# Revit family: Crealco Resistance Side Hung C
name_source: partatom
category: Windows
revit_build: Autodesk Revit 2016 (Build: 20150714_1515(x64)
units: mm (PartAtom-declared; Revit-internal decimal feet)

## family parameters
Always vertical = Yes
Cut with Voids When Loaded = No
Host = Wall
OmniClass Number = 23.30.20.00
OmniClass Title = Windows
Room Calculation Point = No
Shared = No

## types (5) — shared parameters
34mm Mullion Inertia = 3.901
50mm Mullion Inertia = 7.412
60mm Mullion Inertia = 10.935
70mm Mullion Inertia = 16.45
80mm Mullion Inertia = 23.166
90mm Mullion Inertia = 32.891
Default Sill Height = 800 mm
Description = Open Out Secure Window
Fixed Panel Mullion Gap = 15 mm  [stored 0.0492126 ft]
Fixed Panel Side Gap = 29 mm
Fixed Panel Transom Gap = 15 mm  [stored 0.0492126 ft]
Limit Fixed Panel Height Max = 6000 mm  [stored 19.685 ft]
Limit Fixed Panel Height Min = 100 mm  [stored 0.328084 ft]
Limit Fixed Panel Width Max = 6000 mm  [stored 19.685 ft]
Limit Fixed Panel Width Min = 100 mm  [stored 0.328084 ft]
Limit Glazing Thickness Max = 20 mm  [stored 0.0656168 ft]
Limit Glazing Thickness Min = 4 mm  [stored 0.0131234 ft]
Limit Mullion 1 Spacing Min = 230 mm  [stored 0.754593 ft]
Limit Sash Height Min = 200 mm  [stored 0.656168 ft]
Limit Sash Width Min = 200 mm  [stored 0.656168 ft]
Limit Window Height Min = 243 mm
Limit Window Width Min = 589 mm
Manufacturer = Crealco
Max Wind Load = 10000
Model = Resistance
Mullion Width = 20 mm  [stored 0.0656168 ft]
Sash Mullion Gap = 8 mm  [stored 0.0262467 ft]
Sash Offset = 4 mm  [stored 0.0131234 ft]
Sash Side Gap = 22 mm
Sash Transom Gap = 8 mm  [stored 0.0262467 ft]
Standard Mullion Side Gap = 595 mm  [stored 1.9521 ft]
Standard Transom 1 Top Gap = 595 mm  [stored 1.9521 ft]
Standard Transom 2 Top Gap = 582 mm  [stored 1.90945 ft]
Transom Mullion Side Gap = 15 mm  [stored 0.0492126 ft]
Transom Side Gap = 29 mm
URL = https://www.crealco.co.za
Wall Closure = By host
zero-valued in all types: Min Wind Load

## per-type parameters (varying)
| type | Standard Height | Standard Size | Standard Width | Type Comments |
| 1790 x 0890mm (RES-1809SS) | 890 mm  [stored 2.91995 ft] | Yes | 1790 mm  [stored 5.8727 ft] | RES-1809SS |
| User Defined | 890 mm  [stored 2.91995 ft] | No | 1790 mm  [stored 5.8727 ft] | Custom |
| 2390 x 0890mm (RES-2409SS) | 890 mm  [stored 2.91995 ft] | Yes | 2390 mm  [stored 7.84121 ft] | RES-2409SS |
| 2390 x 0890mm (RES-1812SS) | 1190 mm  [stored 3.9042 ft] | Yes | 1790 mm  [stored 5.8727 ft] | RES-1812SS |
| 2390 x 1190mm (RES-2412SS) | 1190 mm  [stored 3.9042 ft] | Yes | 2390 mm  [stored 7.84121 ft] | RES-2412SS |

note: [stored X ft] marks values corroborated as IEEE doubles in the binary element streams (Revit-internal decimal feet)

## geometry (parser evidence)
native form markers: Sweep x29
no freeform markers — native parametric forms only
